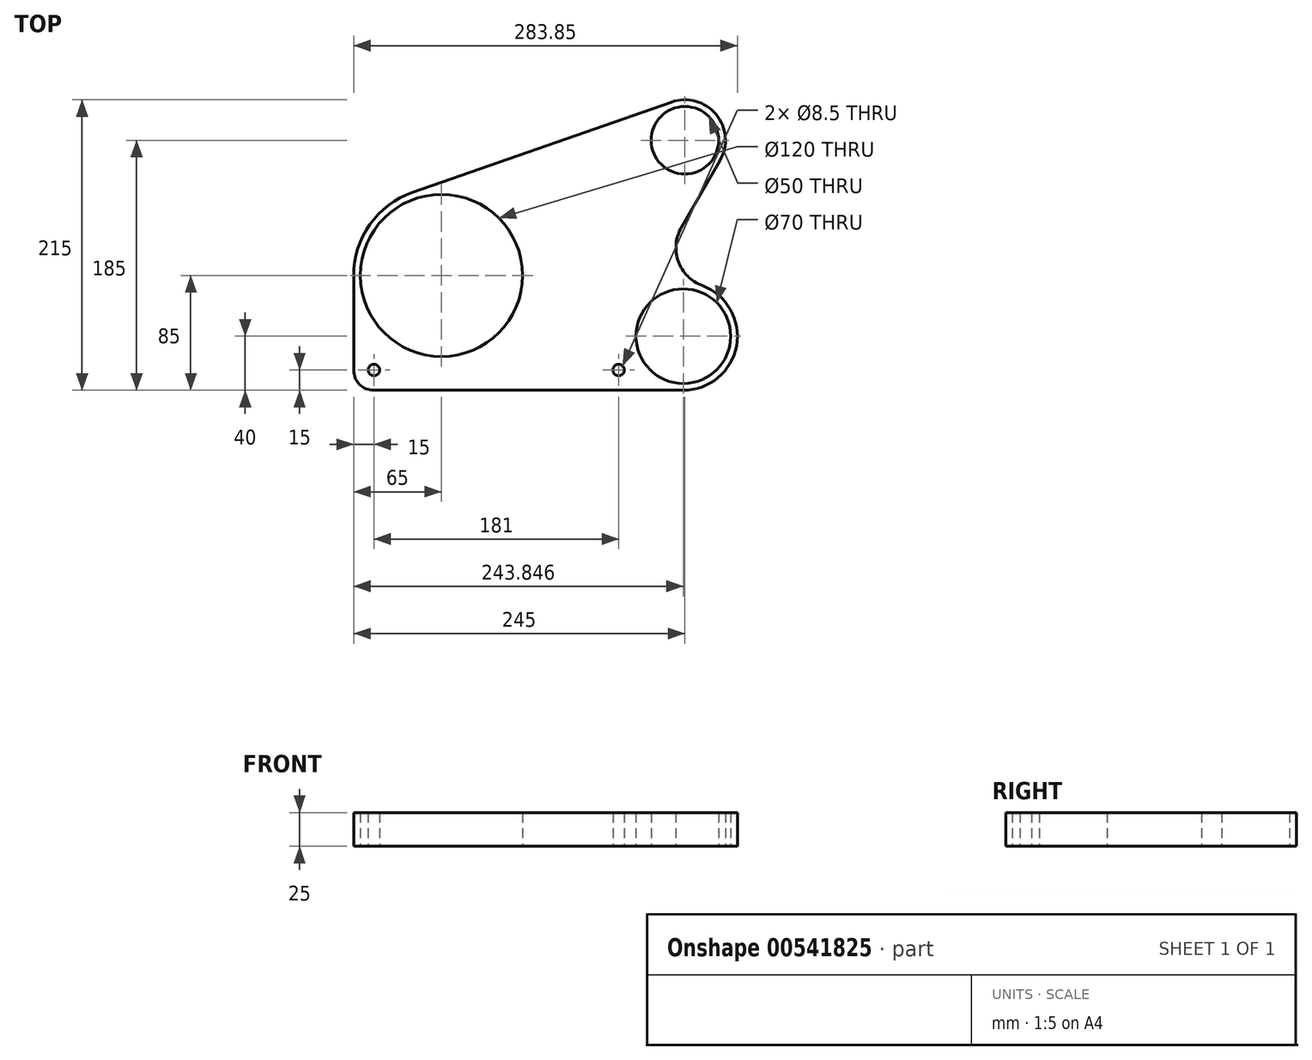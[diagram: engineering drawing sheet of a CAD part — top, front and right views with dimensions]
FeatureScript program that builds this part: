
annotation { "Feature Type Name" : "Feature", "Feature Type Description" : "" }
export const myFeature = defineFeature(function(context is Context, id is Id, definition is map)
    precondition{}
    {
        {
            var Q0;
            Q0=qCreatedBy(makeId("Top.planeOp"),FACE);
            var sketch = newSketch(context, id + "F0", { "sketchPlane" : qUnion([Q0])});
            skCircle(sketch, "E0", {"center": v(0, 0) * mm, "radius": 60 * mm});
            skCircle(sketch, "E1", {"center": v(180, 100) * mm, "radius": 25 * mm});
            skCircle(sketch, "E2", {"center": v(178.85, -45) * mm, "radius": 35 * mm});
            skArc(sketch, "E3.0", {"start": v(-21.45, 61.36) * mm, "mid": v(-53, 37.62) * mm, "end": v(-65, 0) * mm});
            skArc(sketch, "E4.0", {"start": v(150.57, 105.82) * mm, "mid": v(156.9, 80.86) * mm, "end": v(180.24, 70) * mm});
            skArc(sketch, "E5.0", {"start": v(168.94, -6.25) * mm, "mid": v(146.34, -21.7) * mm, "end": v(138.96, -48.05) * mm});
            skLineSegment(sketch, "E6", {"start": v(-65, 0) * mm, "end": v(-65, -70) * mm});
            skLineSegment(sketch, "E7", {"start": v(178.85, -85) * mm, "end": v(-50, -85) * mm});
            skLineSegment(sketch, "E8", {"start": v(-21.45, 61.36) * mm, "end": v(170.1, 128.32) * mm});
            skLineSegment(sketch, "E9", {"start": v(205.98, 85) * mm, "end": v(177.43, 35.55) * mm});
            skArc(sketch, "E10", {"start": v(177.43, 35.55) * mm, "mid": v(175.17, 10.42) * mm, "end": v(192.88, -7.54) * mm});
            skLineSegment(sketch, "E11.0", {"start": v(24.98, 72.3) * mm, "end": v(142.05, 113.22) * mm});
            skArc(sketch, "E12.0", {"start": v(173.1, 38.05) * mm, "mid": v(168.41, 20.67) * mm, "end": v(172.98, 3.26) * mm});
            skLineSegment(sketch, "E12.1", {"start": v(185.92, 60.25) * mm, "end": v(173.1, 38.05) * mm});
            skArc(sketch, "E13.trimOffspring", {"start": v(205.98, 85) * mm, "mid": v(203.1, 119.14) * mm, "end": v(170.1, 128.32) * mm});
            skCircle(sketch, "E14", {"center": v(131, -70) * mm, "radius": 4.25 * mm});
            skArc(sketch, "E15", {"start": v(132.03, -55.04) * mm, "mid": v(119.9, -59.9) * mm, "end": v(116.2, -72.44) * mm});
            skCircle(sketch, "E16", {"center": v(-50, -70) * mm, "radius": 4.25 * mm});
            skArc(sketch, "E17", {"start": v(-35.2, -72.44) * mm, "mid": v(-35, -69.6) * mm, "end": v(-35.35, -66.76) * mm});
            skArc(sketch, "E18", {"start": v(-26.37, -59.4) * mm, "mid": v(-33.12, -60.32) * mm, "end": v(-35.35, -66.76) * mm});
            skLineSegment(sketch, "E19.trimOffspring", {"start": v(109.79, -80) * mm, "end": v(-28.79, -80) * mm});
            skArc(sketch, "E20.trimOffspring", {"start": v(178.85, -85) * mm, "mid": v(218.2, -52.13) * mm, "end": v(192.88, -7.54) * mm});
            skPoint(sketch, "E21.visualSharp", {"position": v(3.8, 64.89) * mm});
            skArc(sketch, "E21.filletArc", {"start": v(24.98, 72.3) * mm, "mid": v(20.62, 66.33) * mm, "end": v(24.66, 60.14) * mm});
            skPoint(sketch, "E22.visualSharp", {"position": v(179.5, -5) * mm});
            skArc(sketch, "E22.filletArc", {"start": v(168.94, -6.25) * mm, "mid": v(173.3, -2.5) * mm, "end": v(172.98, 3.26) * mm});
            skPoint(sketch, "E23.visualSharp", {"position": v(193.36, 73.14) * mm});
            skArc(sketch, "E23.filletArc", {"start": v(185.92, 60.25) * mm, "mid": v(185.9, 66.77) * mm, "end": v(180.24, 70) * mm});
            skPoint(sketch, "E24.visualSharp", {"position": v(119.82, -80) * mm});
            skArc(sketch, "E24.filletArc", {"start": v(109.79, -80) * mm, "mid": v(114.74, -77.7) * mm, "end": v(116.2, -72.44) * mm});
            skPoint(sketch, "E25.visualSharp", {"position": v(-38.82, -80) * mm});
            skArc(sketch, "E25.filletArc", {"start": v(-35.2, -72.44) * mm, "mid": v(-33.74, -77.7) * mm, "end": v(-28.79, -80) * mm});
            skPoint(sketch, "E26.visualSharp", {"position": v(156.1, 118.13) * mm});
            skArc(sketch, "E26.filletArc", {"start": v(150.57, 105.82) * mm, "mid": v(148.45, 111.99) * mm, "end": v(142.05, 113.22) * mm});
            skPoint(sketch, "E27.visualSharp", {"position": v(141.48, -59.26) * mm});
            skArc(sketch, "E27.filletArc", {"start": v(132.03, -55.04) * mm, "mid": v(137.1, -53.13) * mm, "end": v(138.96, -48.05) * mm});
            skCircle(sketch, "E28", {"center": v(30, 0) * mm, "radius": 5 * mm});
            skCircle(sketch, "E29.1.0", {"center": v(15, 25.98) * mm, "radius": 5 * mm});
            skCircle(sketch, "E29.2.0", {"center": v(-15, 25.98) * mm, "radius": 5 * mm});
            skCircle(sketch, "E29.3.0", {"center": v(-30, 0) * mm, "radius": 5 * mm});
            skCircle(sketch, "E29.4.0", {"center": v(-15, -25.98) * mm, "radius": 5 * mm});
            skCircle(sketch, "E29.5.0", {"center": v(15, -25.98) * mm, "radius": 5 * mm});
            skCircle(sketch, "E30", {"center": v(0, 0) * mm, "radius": 50 * mm, "construction": true});
            skArc(sketch, "E31.0", {"start": v(-54.16, -9.55) * mm, "mid": v(-38.9, -38.9) * mm, "end": v(-9.55, -54.16) * mm});
            skArc(sketch, "E32.0", {"start": v(-7.81, 44.32) * mm, "mid": v(-31.82, 31.82) * mm, "end": v(-44.32, 7.81) * mm});
            skArc(sketch, "E33.0", {"start": v(-9.55, 54.16) * mm, "mid": v(-38.9, 38.9) * mm, "end": v(-54.16, 9.55) * mm, "construction": true});
            skLineSegment(sketch, "E34", {"start": v(49.24, 8.68) * mm, "end": v(0, 0) * mm, "construction": true});
            skLineSegment(sketch, "E35", {"start": v(0, 0) * mm, "end": v(50, 0) * mm, "construction": true});
            skArc(sketch, "E36", {"start": v(9.55, 54.16) * mm, "mid": v(3.76, 50.1) * mm, "end": v(7.81, 44.32) * mm});
            skLineSegment(sketch, "E37", {"start": v(8.68, 49.24) * mm, "end": v(0, 0) * mm, "construction": true});
            skLineSegment(sketch, "E38", {"start": v(0, 0) * mm, "end": v(0, 50) * mm, "construction": true});
            skArc(sketch, "E39.MirrorC", {"start": v(-44.32, 7.81) * mm, "mid": v(-50.1, 3.76) * mm, "end": v(-54.16, 9.55) * mm});
            skArc(sketch, "E40.MirrorC", {"start": v(-9.55, 54.16) * mm, "mid": v(-3.76, 50.1) * mm, "end": v(-7.81, 44.32) * mm});
            skArc(sketch, "E41.MirrorC", {"start": v(44.32, 7.81) * mm, "mid": v(50.1, 3.76) * mm, "end": v(54.16, 9.55) * mm});
            skArc(sketch, "E42.MirrorC", {"start": v(44.32, -7.81) * mm, "mid": v(50.1, -3.76) * mm, "end": v(54.16, -9.55) * mm});
            skArc(sketch, "E43.MirrorC", {"start": v(9.55, -54.16) * mm, "mid": v(3.76, -50.1) * mm, "end": v(7.81, -44.32) * mm});
            skArc(sketch, "E44.MirrorC", {"start": v(-9.55, -54.16) * mm, "mid": v(-3.76, -50.1) * mm, "end": v(-7.81, -44.32) * mm});
            skArc(sketch, "E45.MirrorC", {"start": v(-44.32, -7.81) * mm, "mid": v(-50.1, -3.76) * mm, "end": v(-54.16, -9.55) * mm});
            skArc(sketch, "E46.trimOffspring", {"start": v(-44.32, -7.81) * mm, "mid": v(-31.82, -31.82) * mm, "end": v(-7.81, -44.32) * mm});
            skArc(sketch, "E47.trimOffspring", {"start": v(-54.16, -9.55) * mm, "mid": v(-38.9, -38.9) * mm, "end": v(-9.55, -54.16) * mm, "construction": true});
            skArc(sketch, "E48.trimOffspring", {"start": v(7.81, -44.32) * mm, "mid": v(31.82, -31.82) * mm, "end": v(44.32, -7.81) * mm});
            skArc(sketch, "E49.trimOffspring", {"start": v(9.55, -54.16) * mm, "mid": v(38.9, -38.9) * mm, "end": v(54.16, -9.55) * mm, "construction": true});
            skArc(sketch, "E50.trimOffspring", {"start": v(54.16, 9.55) * mm, "mid": v(38.9, 38.9) * mm, "end": v(9.55, 54.16) * mm, "construction": true});
            skArc(sketch, "E51.trimOffspring", {"start": v(45, 0) * mm, "mid": v(34.47, 28.93) * mm, "end": v(7.81, 44.32) * mm});
            skArc(sketch, "E52.trimOffspring", {"start": v(9.55, -54.16) * mm, "mid": v(38.9, -38.9) * mm, "end": v(54.16, -9.55) * mm});
            skArc(sketch, "E53.trimOffspring", {"start": v(54.16, 9.55) * mm, "mid": v(38.9, 38.9) * mm, "end": v(9.55, 54.16) * mm});
            skArc(sketch, "E54.trimOffspring", {"start": v(-9.55, 54.16) * mm, "mid": v(-38.9, 38.9) * mm, "end": v(-54.16, 9.55) * mm});
            skPoint(sketch, "E55.visualSharp", {"position": v(-65, -85) * mm});
            skArc(sketch, "E55.filletArc", {"start": v(-65, -70) * mm, "mid": v(-60.6, -80.6) * mm, "end": v(-50, -85) * mm});
            skArc(sketch, "E56.trimOffspring", {"start": v(-26.37, -59.4) * mm, "mid": v(59.78, -25.52) * mm, "end": v(24.66, 60.14) * mm});
            skSolve(sketch);
        }
        {
            var Q0;
            Q0=makeQuery(id+"F0.imprint","IMPRINT",FACE,{"disambiguationData":[TD([[makeQuery(id+"F0.imprint","IMPRINT",EDGE,{"derivedFrom":sQuery(id+"F0.wireOp",EDGE,"E4.0")}),-1.0]])]});
            var Q1;
            Q1=makeQuery(id+"F0.imprint","IMPRINT",FACE,{"disambiguationData":[TD([[makeQuery(id+"F0.imprint","IMPRINT",EDGE,{"derivedFrom":sQuery(id+"F0.wireOp",EDGE,"E0")}),-1.0]])]});
            extrude(context, id + "F1", {"entities" : qUnion([Q0, Q1]), "depth" : 25 * mm, "offsetDistance" : 25 * mm});
        }
    });
